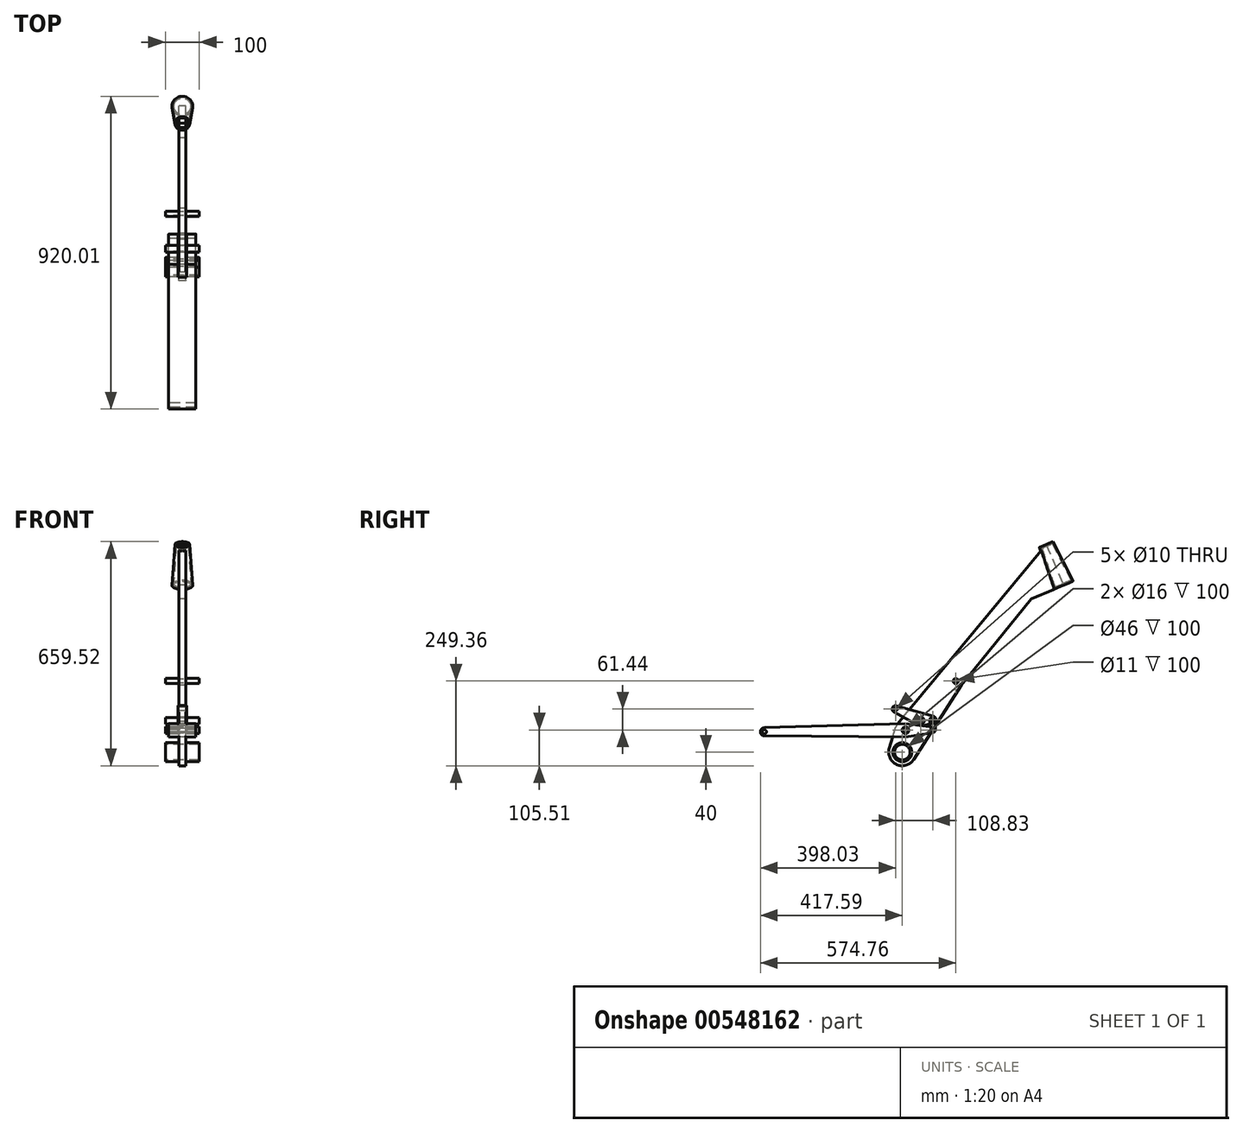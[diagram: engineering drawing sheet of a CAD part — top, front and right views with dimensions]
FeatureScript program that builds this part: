
annotation { "Feature Type Name" : "Feature", "Feature Type Description" : "" }
export const myFeature = defineFeature(function(context is Context, id is Id, definition is map)
    precondition{}
    {
        {
            var Q0;
            Q0=qCreatedBy(makeId("Right.planeOp"),FACE);
            var sketch = newSketch(context, id + "F0", { "sketchPlane" : qUnion([Q0])});
            skLineSegment(sketch, "E0", {"start": v(0, 0) * mm, "end": v(-93.36, 219.95) * mm, "construction": true});
            skLineSegment(sketch, "E1", {"start": v(-323.73, 632.13) * mm, "end": v(-11.64, -103.1) * mm, "construction": true});
            skPoint(sketch, "E2", {"position": v(-238.4, 431.12) * mm});
            skLineSegment(sketch, "E3", {"start": v(-303.73, 403.4) * mm, "end": v(-173.08, 458.85) * mm, "construction": true});
            skCircle(sketch, "E4", {"center": v(0, -8.13) * mm, "radius": 375.7 * mm, "construction": true});
            skPoint(sketch, "E5", {"position": v(-289.3, 551) * mm});
            skPoint(sketch, "E6", {"position": v(-712.3, -60) * mm});
            skPoint(sketch, "E7", {"position": v(-1117.88, 0) * mm});
            skLineSegment(sketch, "E8", {"start": v(-1117.88, 0) * mm, "end": v(0, 0) * mm, "construction": true});
            skCircle(sketch, "E9", {"center": v(-1117.88, 0) * mm, "radius": 375.7 * mm, "construction": true});
            skLineSegment(sketch, "E10", {"start": v(-712.3, -60) * mm, "end": v(-933.24, 662.68) * mm, "construction": true});
            skLineSegment(sketch, "E11", {"start": v(-289.3, 551) * mm, "end": v(-947.84, 551) * mm, "construction": true});
            skPoint(sketch, "E12", {"position": v(-899.1, 551) * mm});
            skLineSegment(sketch, "E13", {"start": v(-237.36, 573.04) * mm, "end": v(-341.22, 528.96) * mm, "construction": true});
            skPoint(sketch, "E14", {"position": v(-277.57, 523.38) * mm});
            skLineSegment(sketch, "E15", {"start": v(-712.3, -60) * mm, "end": v(-277.57, 523.38) * mm, "construction": true});
            skPoint(sketch, "E16", {"position": v(-814.62, 274.7) * mm});
            skLineSegment(sketch, "E17", {"start": v(-814.62, 274.7) * mm, "end": v(-277.57, 523.38) * mm, "construction": true});
            skPoint(sketch, "E18", {"position": v(-546.1, 399.05) * mm});
            skSolve(sketch);
        }
        {
            var Q0;
            Q0=qCreatedBy(makeId("Right.planeOp"),FACE);
            var sketch = newSketch(context, id + "F1", { "sketchPlane" : qUnion([Q0])});
            skLineSegment(sketch, "E19", {"start": v(-262.34, 420.96) * mm, "end": v(-264.3, 425.56) * mm});
            skLineSegment(sketch, "E20", {"start": v(-303.45, 539.56) * mm, "end": v(-264.3, 425.56) * mm});
            skLineSegment(sketch, "E21", {"start": v(-303.45, 539.56) * mm, "end": v(-305.4, 544.16) * mm});
            skLineSegment(sketch, "E22", {"start": v(-305.4, 544.16) * mm, "end": v(-309.35, 542.48) * mm});
            skLineSegment(sketch, "E23", {"start": v(-309.35, 542.48) * mm, "end": v(-266.94, 419) * mm});
            skLineSegment(sketch, "E24", {"start": v(-266.94, 419) * mm, "end": v(-262.34, 420.96) * mm});
            skSolve(sketch);
        }
        {
            var Q0;
            Q0=qSketchRegion(id+"F1",true);
            var Q1;
            Q1=sQuery(id+"F0.wireOp",EDGE,"E1");
            revolve(context, id + "F2", {"entities" : qUnion([Q0]), "axis" : qUnion([Q1]), "revolveType" : RevolveType.FULL});
        }
        {
            var Q0;
            Q0=qCreatedBy(makeId("Right.planeOp"),FACE);
            var sketch = newSketch(context, id + "F3", { "sketchPlane" : qUnion([Q0])});
            skCircle(sketch, "E25", {"center": v(-712.3, -60) * mm, "radius": 23 * mm});
            skCircle(sketch, "E26", {"center": v(-712.3, -60) * mm, "radius": 28 * mm});
            skSolve(sketch);
        }
        {
            var Q0;
            Q0=qSketchRegion(id+"F3",true);
            extrude(context, id + "F4", {"entities" : qUnion([Q0]), "operationType" : NewBodyOperationType.ADD, "endBound" : BoundingType.SYMMETRIC, "depth" : 100 * mm});
        }
        {
            var Q0;
            Q0=qCreatedBy(makeId("Right.planeOp"),FACE);
            var sketch = newSketch(context, id + "F5", { "sketchPlane" : qUnion([Q0])});
            skPoint(sketch, "E27", {"position": v(-703.01, 4.62) * mm});
            skPoint(sketch, "E28", {"position": v(-657.88, 32.46) * mm});
            skPoint(sketch, "E29", {"position": v(-555.12, 149.36) * mm});
            skPoint(sketch, "E30", {"position": v(-623.02, 5.51) * mm});
            skSolve(sketch);
        }
        {
            var Q0;
            Q0=qCreatedBy(makeId("Right.planeOp"),FACE);
            var sketch = newSketch(context, id + "F6", { "sketchPlane" : qUnion([Q0])});
            skArc(sketch, "E31", {"start": v(-750.55, -48.32) * mm, "mid": v(-729.04, -96.33) * mm, "end": v(-678.56, -81.5) * mm});
            skLineSegment(sketch, "E32", {"start": v(-332.3, 391.27) * mm, "end": v(-238.4, 431.12) * mm});
            skLineSegment(sketch, "E33", {"start": v(-289.3, 551) * mm, "end": v(-238.4, 431.12) * mm});
            skCircle(sketch, "E34", {"center": v(-712.3, -60) * mm, "radius": 28 * mm});
            skArc(sketch, "E35", {"start": v(-726.11, 23.76) * mm, "mid": v(-729.42, 18.85) * mm, "end": v(-731.7, 13.38) * mm});
            skLineSegment(sketch, "E36.trimOffspring", {"start": v(-726.11, 23.76) * mm, "end": v(-289.3, 551) * mm});
            skCircle(sketch, "E37", {"center": v(-657.88, 32.46) * mm, "radius": 10 * mm});
            skCircle(sketch, "E38", {"center": v(-703.01, 4.62) * mm, "radius": 10 * mm});
            skCircle(sketch, "E39", {"center": v(-555.12, 149.36) * mm, "radius": 7.5 * mm});
            skArc(sketch, "E40", {"start": v(-538.25, 138.6) * mm, "mid": v(-571.33, 161.07) * mm, "end": v(-539.61, 136.73) * mm});
            skLineSegment(sketch, "E41", {"start": v(-332.3, 391.27) * mm, "end": v(-539.61, 136.73) * mm});
            skLineSegment(sketch, "E42", {"start": v(-678.56, -81.5) * mm, "end": v(-538.25, 138.6) * mm});
            skLineSegment(sketch, "E43", {"start": v(-750.55, -48.32) * mm, "end": v(-731.7, 13.38) * mm});
            skSolve(sketch);
        }
        {
            var Q0;
            Q0=qSketchRegion(id+"F6",true);
            extrude(context, id + "F7", {"entities" : qUnion([Q0]), "operationType" : NewBodyOperationType.ADD, "endBound" : BoundingType.SYMMETRIC, "depth" : 20 * mm});
        }
        {
            var Q0;
            Q0=qCreatedBy(makeId("Right.planeOp"),FACE);
            var sketch = newSketch(context, id + "F8", { "sketchPlane" : qUnion([Q0])});
            skCircle(sketch, "E44", {"center": v(-555.12, 149.36) * mm, "radius": 7.5 * mm});
            skCircle(sketch, "E45", {"center": v(-703.01, 4.62) * mm, "radius": 10 * mm});
            skCircle(sketch, "E46", {"center": v(-657.88, 32.46) * mm, "radius": 10 * mm});
            skCircle(sketch, "E47", {"center": v(-555.12, 149.36) * mm, "radius": 5.5 * mm});
            skCircle(sketch, "E48", {"center": v(-703.01, 4.62) * mm, "radius": 8 * mm});
            skCircle(sketch, "E49", {"center": v(-657.88, 32.46) * mm, "radius": 8 * mm});
            skSolve(sketch);
        }
        {
            var Q0;
            Q0=qSketchRegion(id+"F8",true);
            extrude(context, id + "F9", {"entities" : qUnion([Q0]), "operationType" : NewBodyOperationType.ADD, "endBound" : BoundingType.SYMMETRIC, "depth" : 100 * mm});
        }
        {
            var Q0;
            Q0=qCreatedBy(makeId("Right.planeOp"),FACE);
            var sketch = newSketch(context, id + "F10", { "sketchPlane" : qUnion([Q0])});
            skLineSegment(sketch, "E50", {"start": v(-1117.97, -12) * mm, "end": v(-703.17, -15.38) * mm});
            skCircle(sketch, "E51", {"center": v(-1117.88, 0) * mm, "radius": 6 * mm});
            skCircle(sketch, "E52", {"center": v(-703.01, 4.62) * mm, "radius": 10 * mm});
            skArc(sketch, "E53", {"start": v(-1118.24, 12) * mm, "mid": v(-1129.88, -0.13) * mm, "end": v(-1117.97, -12) * mm});
            skLineSegment(sketch, "E54", {"start": v(-1118.24, 12) * mm, "end": v(-703.62, 24.61) * mm});
            skCircle(sketch, "E55", {"center": v(-623.02, 5.51) * mm, "radius": 5 * mm});
            skLineSegment(sketch, "E56", {"start": v(-703.62, 24.61) * mm, "end": v(-621.94, 13.44) * mm});
            skLineSegment(sketch, "E57", {"start": v(-703.17, -15.38) * mm, "end": v(-621.76, -2.4) * mm});
            skArc(sketch, "E58", {"start": v(-621.76, -2.4) * mm, "mid": v(-615.02, 5.6) * mm, "end": v(-621.94, 13.44) * mm});
            skSolve(sketch);
        }
        {
            var Q0;
            Q0=qSketchRegion(id+"F10",true);
            extrude(context, id + "F11", {"entities" : qUnion([Q0]), "endBound" : BoundingType.SYMMETRIC, "depth" : 80 * mm, "offsetDistance" : 25 * mm});
        }
        {
            var Q0;
            Q0=qCreatedBy(makeId("Right.planeOp"),FACE);
            var sketch = newSketch(context, id + "F12", { "sketchPlane" : qUnion([Q0])});
            skPoint(sketch, "E59", {"position": v(-731.85, 66.95) * mm});
            skPoint(sketch, "E60", {"position": v(-623.02, 35.51) * mm});
            skArc(sketch, "E61", {"start": v(-729.07, 76.56) * mm, "mid": v(-741.1, 70.75) * mm, "end": v(-736.62, 58.16) * mm});
            skArc(sketch, "E62", {"start": v(-665.04, 19.28) * mm, "mid": v(-659.88, 17.6) * mm, "end": v(-654.45, 17.86) * mm});
            skArc(sketch, "E63", {"start": v(-620.73, 25.77) * mm, "mid": v(-613.02, 35.26) * mm, "end": v(-620.24, 45.12) * mm});
            skCircle(sketch, "E64", {"center": v(-731.85, 66.95) * mm, "radius": 5 * mm});
            skCircle(sketch, "E65", {"center": v(-623.02, 35.51) * mm, "radius": 5 * mm});
            skLineSegment(sketch, "E66", {"start": v(-654.45, 17.86) * mm, "end": v(-620.73, 25.77) * mm});
            skLineSegment(sketch, "E67", {"start": v(-620.24, 45.12) * mm, "end": v(-729.07, 76.56) * mm});
            skLineSegment(sketch, "E68", {"start": v(-736.62, 58.16) * mm, "end": v(-665.04, 19.28) * mm});
            skCircle(sketch, "E69", {"center": v(-657.88, 32.46) * mm, "radius": 10 * mm});
            skSolve(sketch);
        }
        {
            var Q0;
            Q0=qSketchRegion(id+"F12",true);
            extrude(context, id + "F13", {"entities" : qUnion([Q0]), "endBound" : BoundingType.SYMMETRIC, "depth" : 25 * mm});
        }
        {
            var Q0;
            Q0=qCreatedBy(makeId("Right.planeOp"),FACE);
            var sketch = newSketch(context, id + "F14", { "sketchPlane" : qUnion([Q0])});
            skLineSegment(sketch, "E70.left", {"start": v(-631.02, 35.51) * mm, "end": v(-631.02, 5.51) * mm});
            skLineSegment(sketch, "E70.right", {"start": v(-615.02, 35.51) * mm, "end": v(-615.02, 5.51) * mm});
            skArc(sketch, "E71", {"start": v(-615.02, 35.51) * mm, "mid": v(-623.02, 43.51) * mm, "end": v(-631.02, 35.51) * mm});
            skArc(sketch, "E72", {"start": v(-631.02, 5.51) * mm, "mid": v(-623.02, -2.49) * mm, "end": v(-615.02, 5.51) * mm});
            skCircle(sketch, "E73", {"center": v(-623.02, 35.51) * mm, "radius": 5 * mm});
            skCircle(sketch, "E74", {"center": v(-623.02, 5.51) * mm, "radius": 5 * mm});
            skSolve(sketch);
        }
        {
            var Q0;
            Q0 = qSketchRegion(id + "F14", true);
            extrude(context, id + "F15", {"entities" : qUnion([Q0]), "endBound" : BoundingType.SYMMETRIC, "depth" : 25 * mm, "offsetDistance" : 25 * mm});
        }
    });
